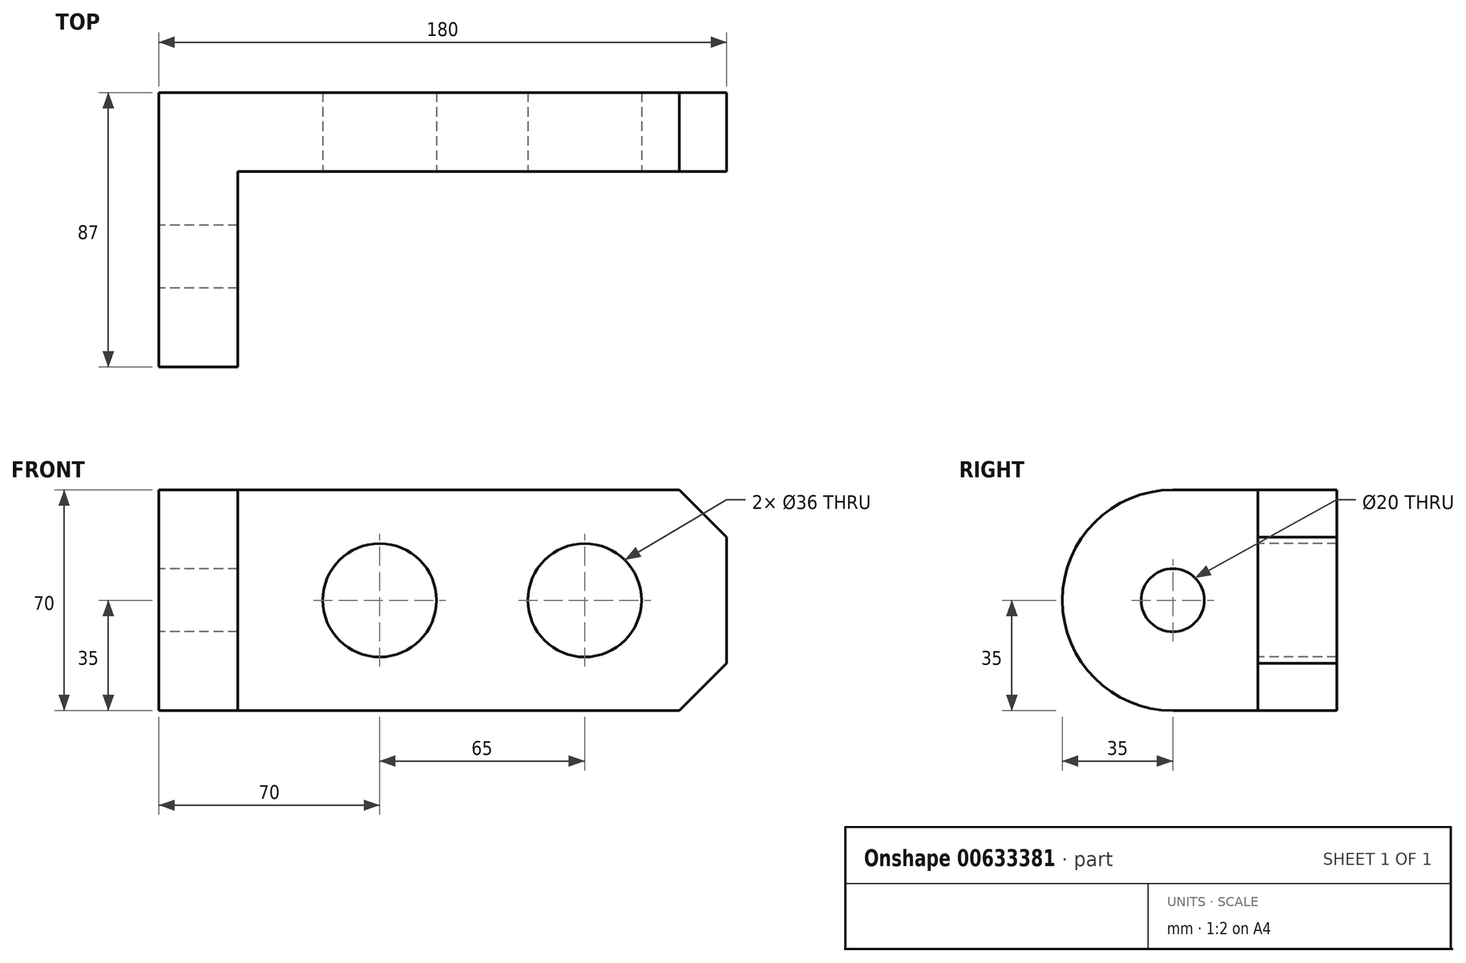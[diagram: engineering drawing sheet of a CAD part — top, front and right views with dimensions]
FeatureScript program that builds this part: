
annotation { "Feature Type Name" : "Feature", "Feature Type Description" : "" }
export const myFeature = defineFeature(function(context is Context, id is Id, definition is map)
    precondition{}
    {
        {
            var Q0;
            Q0=qCreatedBy(makeId("Front.planeOp"),FACE);
            var sketch = newSketch(context, id + "F0", { "sketchPlane" : qUnion([Q0])});
            skLineSegment(sketch, "E0.bottom", {"start": v(90, -35) * mm, "end": v(-90, -35) * mm});
            skLineSegment(sketch, "E0.top", {"start": v(90, 35) * mm, "end": v(-90, 35) * mm});
            skLineSegment(sketch, "E0.left", {"start": v(90, -35) * mm, "end": v(90, 35) * mm});
            skLineSegment(sketch, "E0.right", {"start": v(-90, -35) * mm, "end": v(-90, 35) * mm});
            skPoint(sketch, "E0.middle", {"position": v(0, 0) * mm});
            skCircle(sketch, "E1", {"center": v(-20, 0) * mm, "radius": 18 * mm});
            skCircle(sketch, "E2", {"center": v(45, 0) * mm, "radius": 18 * mm});
            skLineSegment(sketch, "E3", {"start": v(-65, 35) * mm, "end": v(-65, -35) * mm});
            skSolve(sketch);
        }
        {
            var Q0;
            Q0 = qSketchRegion(id + "F0", true);
            extrude(context, id + "F1", {"entities" : qUnion([Q0]), "oppositeDirection" : true, "depth" : 25 * mm, "offsetDistance" : 25.4 * mm});
        }
        {
            var Q0;
            Q0=makeQuery(id+"F1.opExtrude","SWEPT_FACE",FACE,{"disambiguationData":[OSD([sQuery(id+"F0.wireOp",EDGE,"E0.right")])]});
            var sketch = newSketch(context, id + "F2", { "sketchPlane" : qUnion([Q0])});
            skLineSegment(sketch, "E4", {"start": v(-25, 35) * mm, "end": v(27, 35) * mm});
            skLineSegment(sketch, "E5", {"start": v(-25, -35) * mm, "end": v(27, -35) * mm});
            skLineSegment(sketch, "E6", {"start": v(-25, 35) * mm, "end": v(-25, -35) * mm});
            skArc(sketch, "E7", {"start": v(27, -35) * mm, "mid": v(62, 0) * mm, "end": v(27, 35) * mm});
            skCircle(sketch, "E8", {"center": v(27, 0) * mm, "radius": 10 * mm});
            skSolve(sketch);
        }
        {
            var Q0;
            {var subQ2=sQuery(id+"F2.wireOp",EDGE,"E7");Q0=makeQuery(id+"F2.imprint","IMPRINT",FACE,{"disambiguationData":[TD([[makeQuery(id+"F2.imprint","IMPRINT",EDGE,{"derivedFrom":subQ2}),1.0]])]});}
            extrude(context, id + "F3", {"entities" : qUnion([Q0]), "operationType" : NewBodyOperationType.ADD, "oppositeDirection" : true, "depth" : 25 * mm, "offsetDistance" : 25.4 * mm});
        }
        {
            var Q0;
            Q0=makeQuery(id+"F1.opExtrude","SWEPT_EDGE",EDGE,{"disambiguationData":[OSD([sQuery(id+"F0.wireOp",EDGE,"E0.top"),sQuery(id+"F0.wireOp",EDGE,"E0.left")])]});
            var Q1;
            Q1=makeQuery(id+"F1.opExtrude","SWEPT_EDGE",EDGE,{"disambiguationData":[OSD([sQuery(id+"F0.wireOp",EDGE,"E0.bottom"),sQuery(id+"F0.wireOp",EDGE,"E0.left")])]});
            chamfer(context, id + "F4", {"entities" : qUnion([Q0, Q1]), "width" : 15 * mm, "tangentPropagation" : true});
        }
    });
